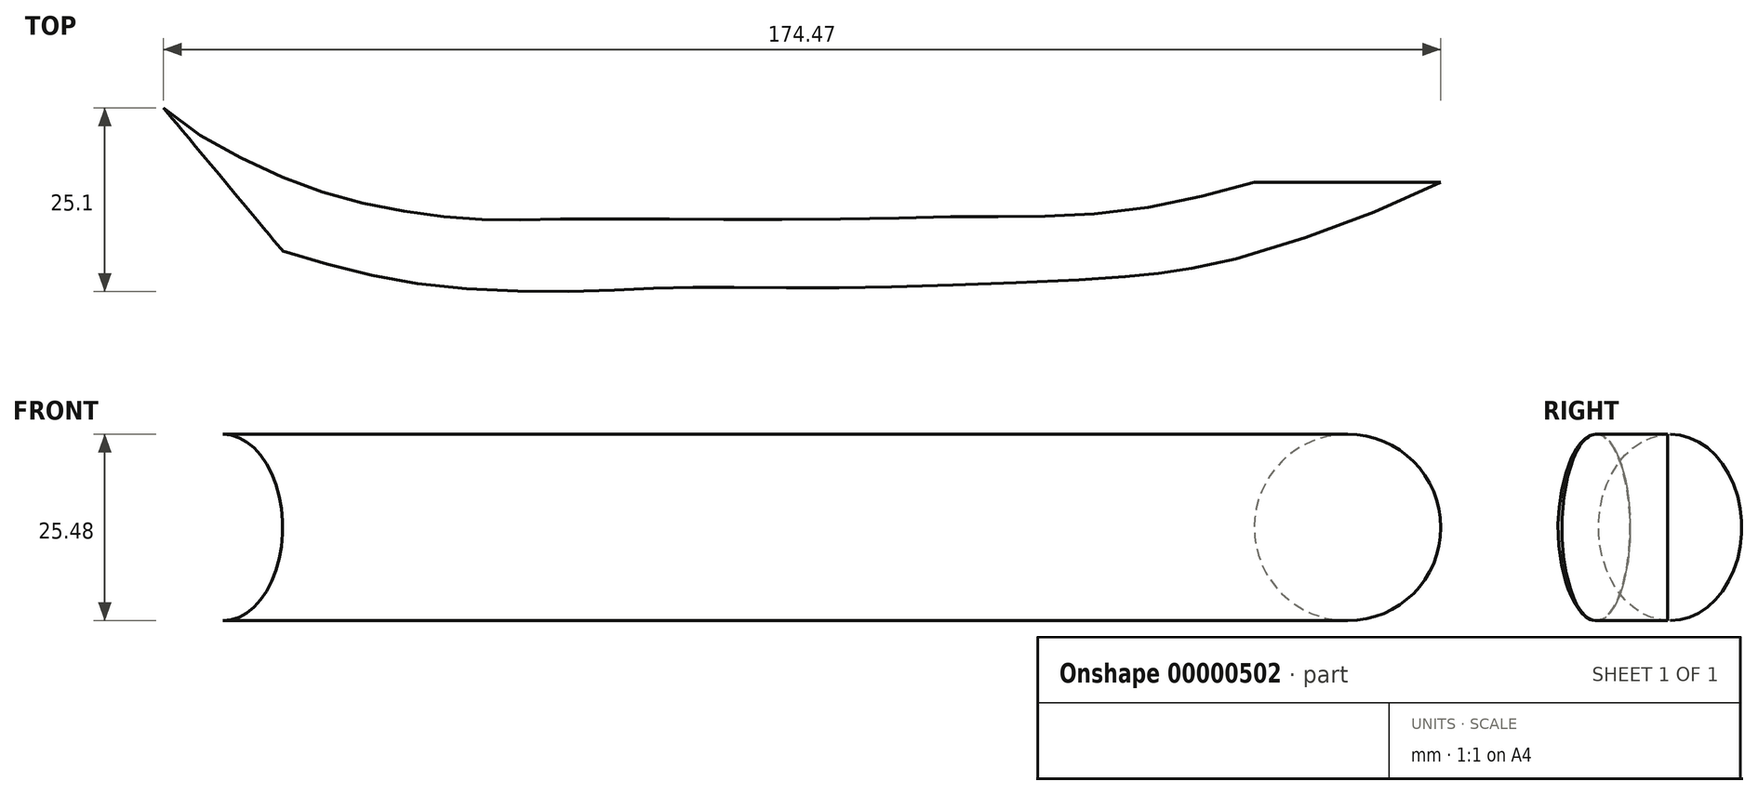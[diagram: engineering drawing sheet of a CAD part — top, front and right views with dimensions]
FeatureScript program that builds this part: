
annotation { "Feature Type Name" : "Feature", "Feature Type Description" : "" }
export const myFeature = defineFeature(function(context is Context, id is Id, definition is map)
    precondition{}
    {
        {
            var Q0;
            Q0=qCreatedBy(makeId("Front.planeOp"),FACE);
            var sketch = newSketch(context, id + "F0", { "sketchPlane" : qUnion([Q0])});
            skCircle(sketch, "E0", {"center": v(76.25, 0) * mm, "radius": 12.74 * mm});
            skSolve(sketch);
        }
        {
            var Q0;
            Q0=qCreatedBy(makeId("Top.planeOp"),FACE);
            var sketch = newSketch(context, id + "F1", { "sketchPlane" : qUnion([Q0])});
            skFitSpline(sketch, "E1", {"points": [v(-77.02, 0) * mm, v(-57.87, -7.18) * mm, v(-37.36, -9.84) * mm, v(-21.17, -9.91) * mm, v(4.58, -9.86) * mm, v(31.27, -9.14) * mm, v(53.22, -6.96) * mm, v(76.73, 0) * mm], "startDerivative": vector(113.57, -61.8) * mm, "endDerivative": vector(148.26, 58.8) * mm});
            skSolve(sketch);
        }
        {
            var Q0;
            Q0=makeQuery(id+"F0.imprint","IMPRINT",FACE,{"disambiguationData":[TD([[makeQuery(id+"F0.imprint","IMPRINT",EDGE,{"derivedFrom":sQuery(id+"F0.wireOp",EDGE,"E0")}),1.0]])]});
            var Q1;
            Q1=sQuery(id+"F1.wireOp",EDGE,"E1");
            sweep(context, id + "F2", {"profiles" : qUnion([Q0]), "path" : qUnion([Q1])});
        }
    });
